# Revit family: Cameo 1.6_A
name_source: partatom
category: Lighting Fixtures
revit_build: Autodesk Revit 2017 (Build: 20170419_0315(x64)
units: mm (PartAtom-declared; Revit-internal decimal feet)

## family parameters
Cut with Voids When Loaded = Yes
Host = Face
Light Source = Yes
Part Type = Normal
Room Calculation Point = Yes
Round Connector Dimension = Use Diameter
Shared = No

## types (5) — shared parameters
Apparent Load = 0 VA
Apparent Load Phase 1 = 3 W
CRI = 90
Code = CM1600100050SN Black; CM1600100050SE White
Color Filter = 16777215
Control system = -
Cutout dimensions = diam. 35 mm
Default Elevation = 1219 mm
Delivered lumen output = 144 lm (3000K, 29°)
Description = Recessed for indoor applications
Dimming Lamp Color Temperature Shift = <None>
Emit from Line Length = 610 mm
Energy efficiency class = A A+ A++
Features = -
Geometry = Cameo1.6_mod
Height Void = 35 mm  [stored 0.114829 ft]
Height mm = 33 mm
IP = 40
LED Colour = 3000K (also available: 2700K and 4000K - ref. URL Technical sheet)
Length mm = 39 mm  [stored 0.127953 ft]
Lens = L&L_Tempered extra-clear glass
Lumen output at source = 157 lm (3000K)
Manufacturer = L&L Luce&Light
Material = body and trim in aluminium
Model = Cameo 1.6
Mounting = recessed (ceilings, and false ceilings and niches in plasterboard)
No. and type of led = 1 power LED, 1/4 ANSI BIN, 50 000h L90 B10 (Ta 25°C)
Notes = -
Power = 2.5W
Power cables = includes 1.5 m PVC cable FROR 2x0.35/0.35 Ø3.5 m
Power supply = 24Vdc
Power supply unit = not included
Radius Void = 15 mm  [stored 0.0492126 ft]
Tilt Angle = 90.00°
Tiltable = -
URL = https://www.lucelight.it
URL Accessories and power supply units = https://www.lucelight.it
URL Catalogue = -
URL DXF = https://www.lucelight.it
URL Description = https://www.lucelight.it
URL General code = https://www.lucelight.it
URL IES Photometric file = https://www.lucelight.it
URL Image = https://www.lucelight.it
URL Technical sheet = https://www.lucelight.it
Voltage = 24 V
Weight kg = 0.07 kg
Width mm = 39 mm  [stored 0.127953 ft]
Wiring = parallel

## per-type parameters (varying)
| type | Body | Optics | Photometric Web File | Springs | Trim |
| Cameo 1.6_L 52° (3000K 2.5W 24Vdc) | L&L_White anodized aluminium | 52° | CAMEO 1.6 L 52° [3000K 2.5W 24Vdc].IES | L&L_C 67 annealed steel | L&L_Anodized aluminium |
| Cameo 1.6_M 29° (3000K 2.5W 24Vdc) | L&L_Anodized aluminium | 29° | CAMEO 1.6 M 29° [3000K 2.5W 24Vdc].IES | <By Category> | L&L_Steel inox AISI 316L |
| Cameo 1.6_P 48° (3000K 2.5W 24Vdc) | L&L_Anodized aluminium | 48° | CAMEO 1.6 P (48°) [3000K 2.5W 24Vdc].IES | <By Category> | L&L_Steel inox AISI 316L |
| Cameo 1.6_S 17° (3000K 2.5W 24Vdc) | L&L_Anodized aluminium | 17° | CAMEO 1.6 S 17° [3000K 2.5W 24Vdc].IES | <By Category> | L&L_Steel inox AISI 316L |
| Cameo 1.6_W 16°x34° (3000K 2.5W 24Vdc) | L&L_Anodized aluminium | 16°x34° | CAMEO 1.6 W 16°x34° [3000K 2.5W 24Vdc].IES | <By Category> | L&L_Steel inox AISI 316L |

note: [stored X ft] marks values corroborated as IEEE doubles in the binary element streams (Revit-internal decimal feet)

## geometry (parser evidence)
native form markers: Blend x2, Sweep x6
no freeform markers — native parametric forms only
